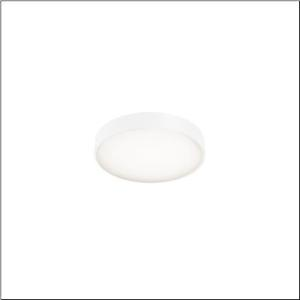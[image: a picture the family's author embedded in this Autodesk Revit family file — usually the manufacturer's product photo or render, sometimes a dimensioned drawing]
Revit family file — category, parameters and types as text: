
# Revit family: round_21_s_51mr34gd0421w
name_source: partatom
category: Lighting Fixtures
units: mm (PartAtom-declared; Revit-internal decimal feet)

## family parameters
Cut with Voids When Loaded = No
Host = Face
Light Source = No
Part Type = Normal
Room Calculation Point = No
Round Connector Dimension = Use Diameter
Shared = No

## types (1)
- Round 21 S (1 x LED, 3490 lm, 28 W, 4000K)
    Apparent Load = 28 VA
    CIE Flux Codes = 49 80 96 79 100
    Color Rendering = 80
    Color Temperature = 4000K
    Default Elevation = 1800 mm
    Description = Round 21 S, wall and ceiling luminaire, primary optical cover: cover, of PMMA, opal, light emission: direct/indirect distribution, primary light characteristic: symmetric, installation type: suspended mounting, surface-mounted, LED, rated luminous flux: 3.580lm, luminous efficacy: 118lm/W, light colour: 840, colour temperature: 4000K, with terminal, 5-pole, mains connection: 230V, AC, 50/60Hz, rated input power: 30W, housing, of aluminium, coated, white, diameter: 400mm, height: 62mm, protection rating (complete): IP40, insulation class (complete): insulation class I (protective earthing), certification: CE, impact resistance: IK04, permissible operating ambient temperature: -10..+35°C, packaging unit: 1 piece
    Height = 87 mm
    Lamp = 1 x LED
    Lamp Light Flux = 3490 lm
    Lamp Power = 28 W
    Lamp count = 1
    Length = 400 mm
    Luminous efficacy = 125 lm/W
    Manufacturer = Siteco
    ModVariant = No
    Model = 51MR34GD0421W
    Mounting Place = Ceiling
    Mounting Type = Surface mounted
    Number of Poles = 1
    OnlyDefault = Yes
    Power Factor = 1
    Product Name = Round 21 S
    Product group = wall and ceiling luminaire
    ProductGroupID = 302
    Protection Class = Protection class I
    Protection Degree = IP 40
    RLX_Detail_Level = 1
    RLX_Emergency_Light_Flux = 0 lm
    RLX_Emergency_Type = 0
    RLX_Emergency_Type_DB = No
    RlxData = <blob elided: 9901 chars, md5=0c64330d>
    Socket = socket
    Standby Power = 0 W
    System Light Flux = 3490 lm
    System Power = 28 W
    Type Comments = Product without accessories
    Type Image = l_1258307.jpg
    URL = http://relux.com
    VarID = ---
    Voltage = 0 V
    Weight = 0.00 kg
    Width = 0 mm  [stored 0 ft]

note: [stored X ft] marks values corroborated as IEEE doubles in the binary element streams (Revit-internal decimal feet)

## geometry (parser evidence)
native form markers: Sweep x11
no freeform markers — native parametric forms only
